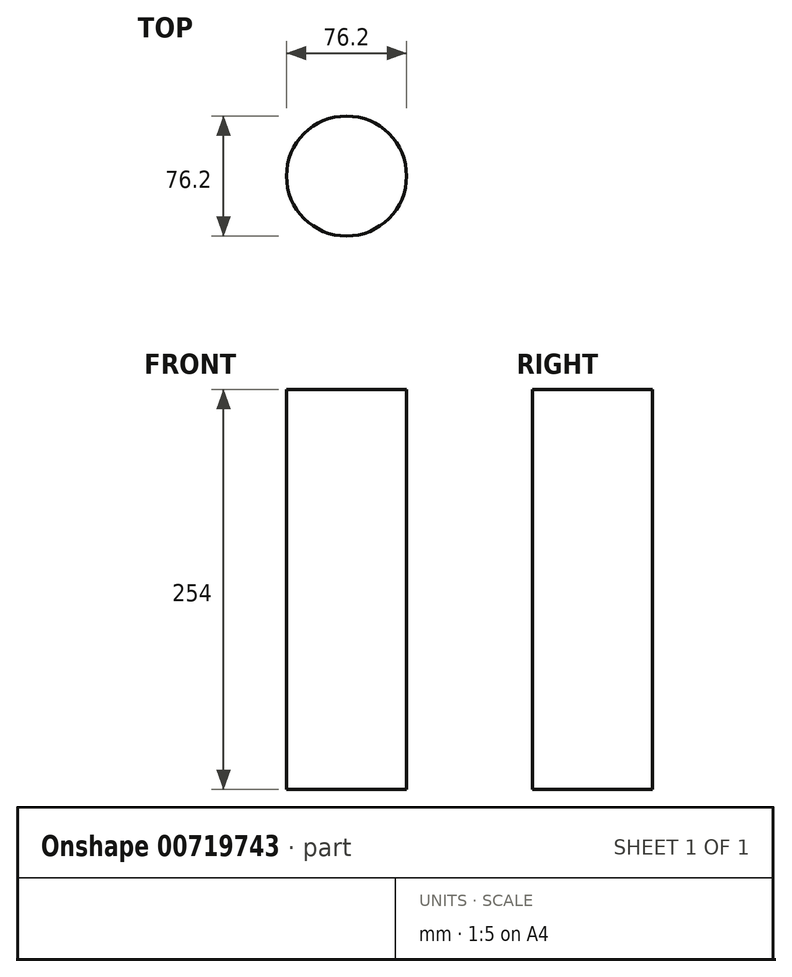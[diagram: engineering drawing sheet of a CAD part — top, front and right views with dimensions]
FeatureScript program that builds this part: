
annotation { "Feature Type Name" : "Feature", "Feature Type Description" : "" }
export const myFeature = defineFeature(function(context is Context, id is Id, definition is map)
    precondition{}
    {
        {
            var Q0;
            Q0=qCreatedBy(makeId("Top.planeOp"),FACE);
            var sketch = newSketch(context, id + "F0", { "sketchPlane" : qUnion([Q0])});
            skCircle(sketch, "E0", {"center": v(0, 0) * mm, "radius": 38.1 * mm});
            skSolve(sketch);
        }
        {
            var Q0;
            Q0 = qSketchRegion(id + "F0", true);
            extrude(context, id + "F1", {"entities" : qUnion([Q0]), "depth" : 254 * mm, "offsetDistance" : 25.4 * mm});
        }
    });
